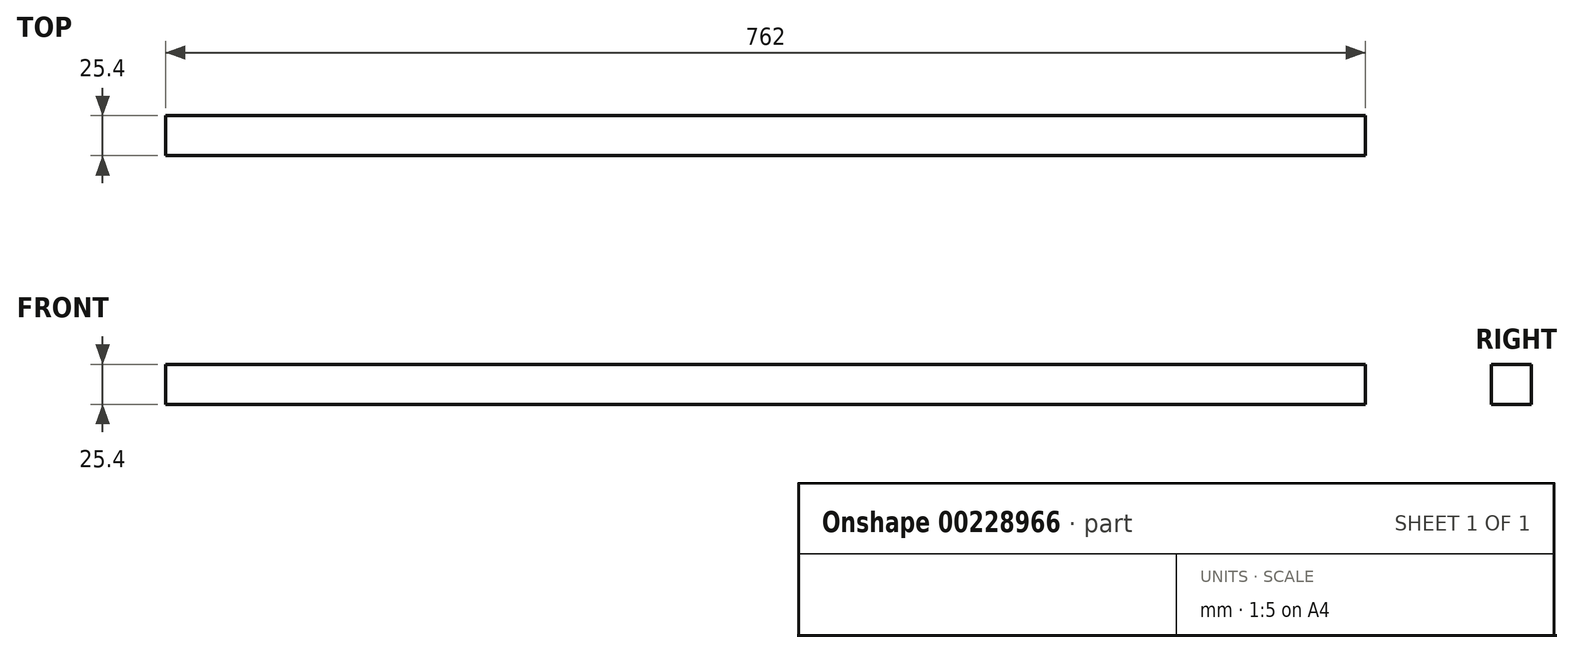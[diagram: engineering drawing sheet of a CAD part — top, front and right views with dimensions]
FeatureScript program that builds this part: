
annotation { "Feature Type Name" : "Feature", "Feature Type Description" : "" }
export const myFeature = defineFeature(function(context is Context, id is Id, definition is map)
    precondition{}
    {
        {
            var Q0;
            Q0=qCreatedBy(makeId("Top.planeOp"),FACE);
            var sketch = newSketch(context, id + "F0", { "sketchPlane" : qUnion([Q0])});
            skLineSegment(sketch, "E0.bottom", {"start": v(0, 0) * mm, "end": v(762, 0) * mm});
            skLineSegment(sketch, "E0.top", {"start": v(0, 25.4) * mm, "end": v(762, 25.4) * mm});
            skLineSegment(sketch, "E0.left", {"start": v(0, 0) * mm, "end": v(0, 25.4) * mm});
            skLineSegment(sketch, "E0.right", {"start": v(762, 0) * mm, "end": v(762, 25.4) * mm});
            skSolve(sketch);
        }
        {
            var Q0;
            Q0 = qSketchRegion(id + "F0", true);
            extrude(context, id + "F1", {"entities" : qUnion([Q0]), "depth" : 25.4 * mm});
        }
    });
